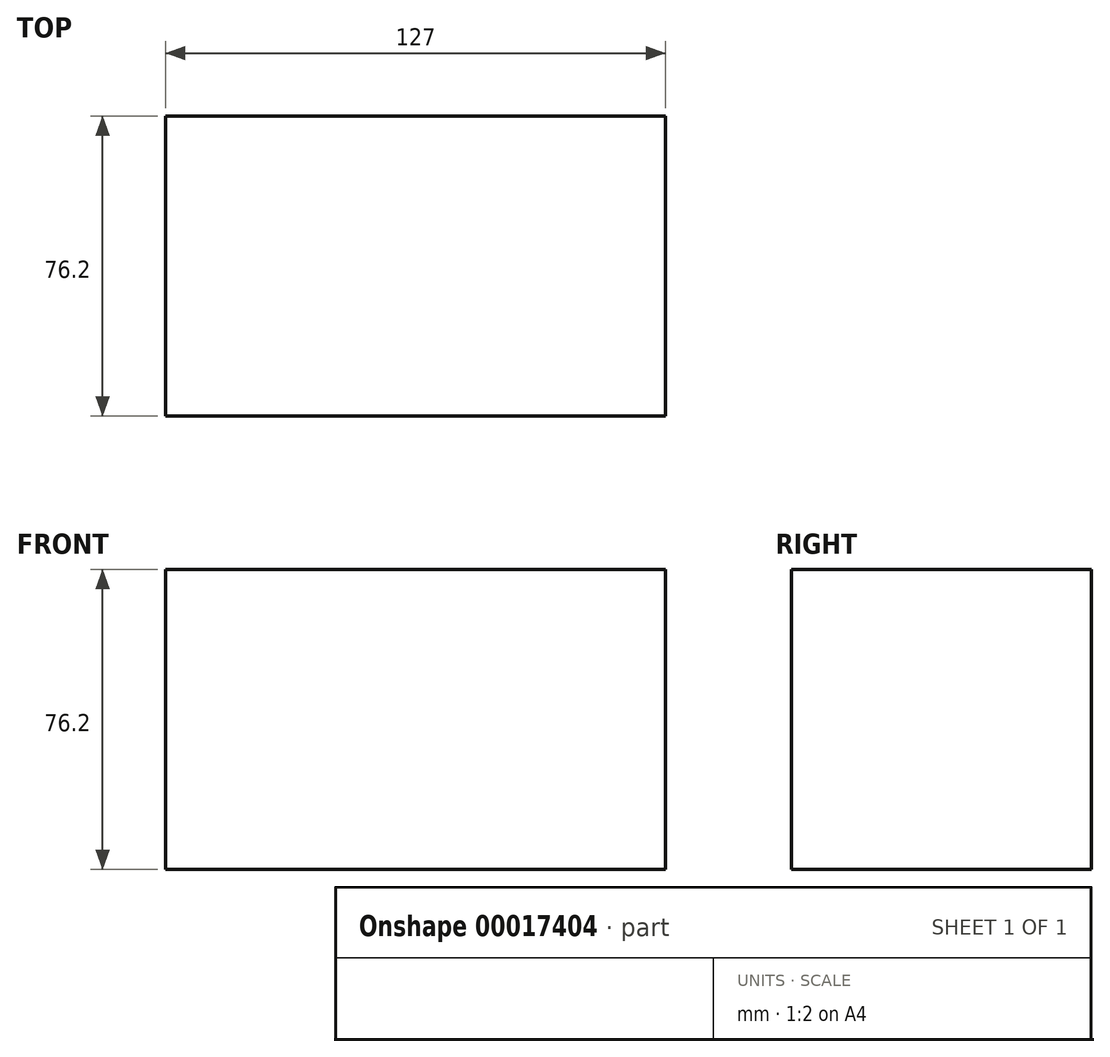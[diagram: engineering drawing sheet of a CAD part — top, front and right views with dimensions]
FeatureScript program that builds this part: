
annotation { "Feature Type Name" : "Feature", "Feature Type Description" : "" }
export const myFeature = defineFeature(function(context is Context, id is Id, definition is map)
    precondition{}
    {
        {
            var Q0;
            Q0=qCreatedBy(makeId("Front.planeOp"),FACE);
            var sketch = newSketch(context, id + "F0", { "sketchPlane" : qUnion([Q0])});
            skLineSegment(sketch, "E0.bottom", {"start": v(76.66, 46.67) * mm, "end": v(-50.34, 46.67) * mm});
            skLineSegment(sketch, "E0.top", {"start": v(76.66, -29.53) * mm, "end": v(-50.34, -29.53) * mm});
            skLineSegment(sketch, "E0.left", {"start": v(76.66, 46.67) * mm, "end": v(76.66, -29.53) * mm});
            skLineSegment(sketch, "E0.right", {"start": v(-50.34, 46.67) * mm, "end": v(-50.34, -29.53) * mm});
            skSolve(sketch);
        }
        {
            var Q0;
            Q0=makeQuery(id+"F0.imprint","IMPRINT",FACE,{"disambiguationData":[TD([[makeQuery(id+"F0.imprint","IMPRINT",EDGE,{"derivedFrom":sQuery(id+"F0.wireOp",EDGE,"E0.bottom")}),1.0]])]});
            extrude(context, id + "F1", {"entities" : qUnion([Q0]), "depth" : 76.2 * mm});
        }
    });
